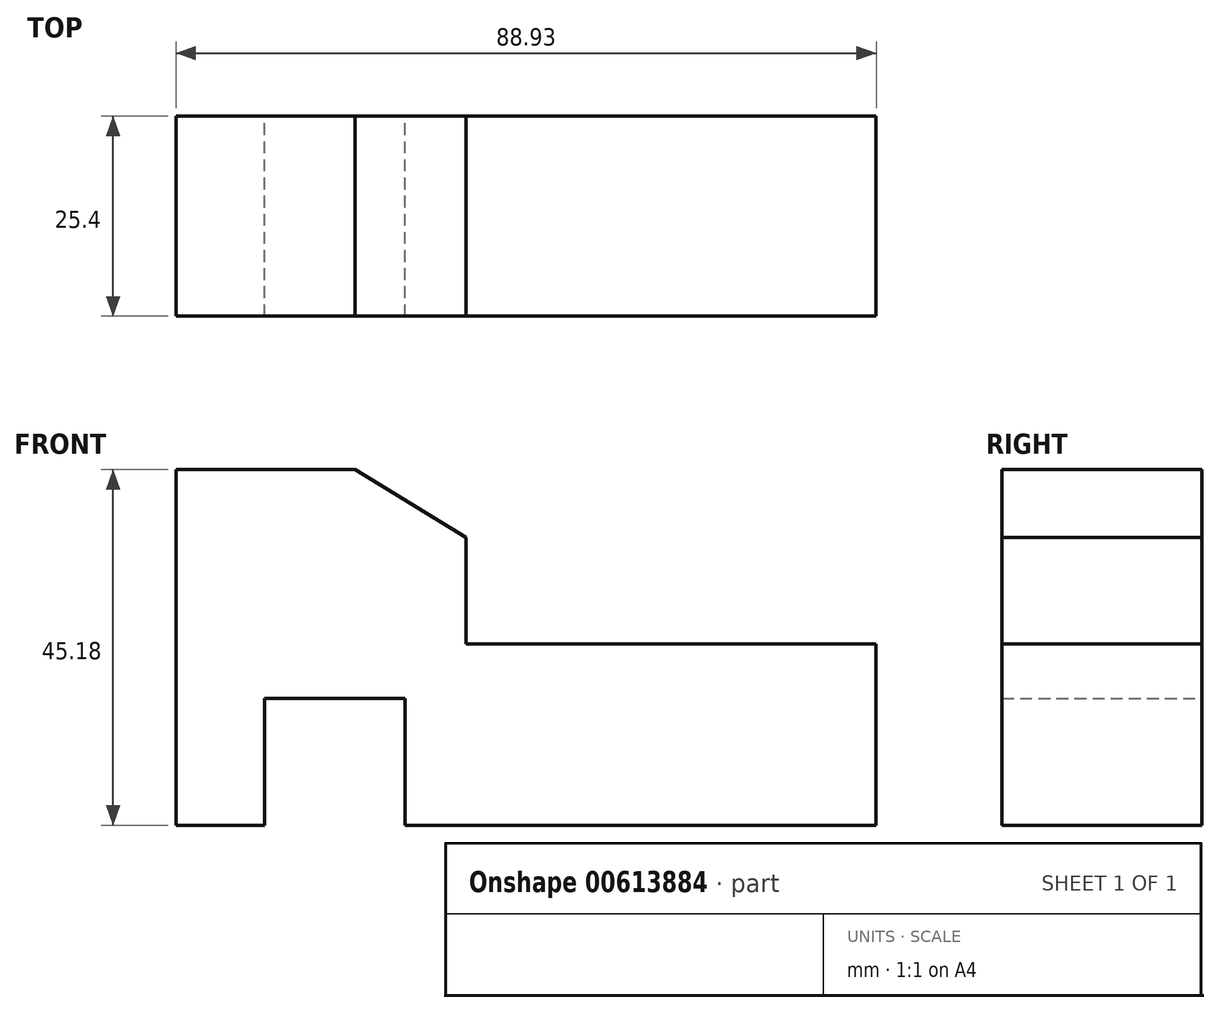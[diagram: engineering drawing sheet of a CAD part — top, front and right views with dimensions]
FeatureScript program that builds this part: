
annotation { "Feature Type Name" : "Feature", "Feature Type Description" : "" }
export const myFeature = defineFeature(function(context is Context, id is Id, definition is map)
    precondition{}
    {
        {
            var Q0;
            Q0=qCreatedBy(makeId("Front.planeOp"),FACE);
            var sketch = newSketch(context, id + "F0", { "sketchPlane" : qUnion([Q0])});
            skLineSegment(sketch, "E0", {"start": v(-65.76, -28.92) * mm, "end": v(-65.76, 16.26) * mm});
            skLineSegment(sketch, "E1", {"start": v(-65.76, 16.26) * mm, "end": v(-65.76, -28.92) * mm});
            skLineSegment(sketch, "E2", {"start": v(-54.54, -28.92) * mm, "end": v(-54.54, -12.8) * mm});
            skLineSegment(sketch, "E3", {"start": v(-54.54, -12.8) * mm, "end": v(-36.7, -12.8) * mm});
            skLineSegment(sketch, "E4", {"start": v(-36.7, -12.8) * mm, "end": v(-36.7, -28.92) * mm});
            skLineSegment(sketch, "E5", {"start": v(-65.76, -28.92) * mm, "end": v(-54.54, -28.92) * mm});
            skLineSegment(sketch, "E6", {"start": v(-36.7, -28.92) * mm, "end": v(23.17, -28.92) * mm});
            skLineSegment(sketch, "E7", {"start": v(23.17, -28.92) * mm, "end": v(23.17, -5.9) * mm});
            skLineSegment(sketch, "E8", {"start": v(23.17, -5.9) * mm, "end": v(-28.92, -5.9) * mm});
            skLineSegment(sketch, "E9", {"start": v(-65.76, 16.26) * mm, "end": v(-43.03, 16.26) * mm});
            skLineSegment(sketch, "E10", {"start": v(-43.03, 16.26) * mm, "end": v(-28.92, 7.63) * mm});
            skLineSegment(sketch, "E11", {"start": v(-28.92, 7.63) * mm, "end": v(-28.92, -5.9) * mm});
            skSolve(sketch);
        }
        {
            var Q0;
            Q0 = qSketchRegion(id + "F0", true);
            extrude(context, id + "F1", {"entities" : qUnion([Q0]), "depth" : 25.4 * mm, "offsetDistance" : 25.4 * mm});
        }
    });
